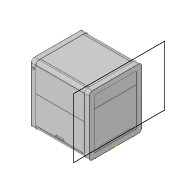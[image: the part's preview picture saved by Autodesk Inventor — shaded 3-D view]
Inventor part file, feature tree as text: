
AUTODESK INVENTOR PART (.ipt)
format: ipt  version: 2019.4 (Build 234330000, 330)  size: 213,504 bytes
history: native  units: mm
features: chamfer x1, sketch x1
ambient origin geometry x8: Origin, YZ Plane, XZ Plane, XY Plane, X Axis, Y Axis, Z Axis, Center Point
bodies: Solid1 (feature_tree)
feature tree (2):
  chamfer  "Chamfer1"  [1 undecoded]
  sketch  "Sketch1"
note: 1 required parameter value undecoded (feature->parameter linkage not recoverable at this tier; creation-order binding heuristic only, values carry confidence <= 0.55)
